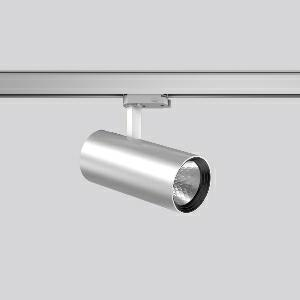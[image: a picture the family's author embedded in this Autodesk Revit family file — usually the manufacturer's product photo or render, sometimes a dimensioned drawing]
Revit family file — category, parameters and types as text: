
# Revit family: deecos_s_mini_742205_004_1_470e
name_source: partatom
category: Lighting Fixtures
units: mm (PartAtom-declared; Revit-internal decimal feet)

## family parameters
Cut with Voids When Loaded = No
Host = Face
Light Source = No
Part Type = Normal
Room Calculation Point = No
Round Connector Dimension = Use Diameter
Shared = No

## types (1)
- DEECOS S mini (1 x LED Modul 940, 3900 lm, 4000)
    Apparent Load = 29 VA
    Approval mark = CE
    CIE Flux Codes = 95 99 100 100 100
    Color Rendering = 92
    Color Temperature = 4000
    Default Elevation = 1800 mm
    Description = Series: DEECOS S mini
LED surface-mounted projector in modern design with no visible cooling ribs. Housing: die-cast aluminium, powder-coated. Rotation range: 356°. Swivel range: 90°. Black plastic ring and recessed LED to prevent glare from the side. Optical assembly with reflector made of MIRO-Silver with 98% total light reflection for outstanding efficiency - can be changed without tools. Best colour rendering index Ra>90. With multi adaptor for 3-circuit tracks 230 V. Suitable for Track on ceiling, Wall track. High quality converter without flickering and stroboscopic effect. The following accessories can be mounted without use of tools: interchangeable lenses, decorative glasses, honeycomb louvre, clear and frosted diffusers, white interchangeable plastic ring. 
Colour: silver
Diameter: 87 mm
Height: 214 mm
Lamp: LED
Socket: without socket
Colour temperature: 4000K
Colour rendering index (CRI): 92
System power: 29 W
Rated luminous flux: 3900 lm
Luminous efficiency: 134 lm/W
Control gear: Regulated power supply
Protection class: I
Type of protection: IP 20
    Height = 214 mm
    Lamp = 1 x LED Modul 940
    Lamp Light Flux = 3900 lm
    Lamp count = 1
    Length = 87 mm
    Lifetime = 50000 h
    Luminous efficacy = 134 lm/W
    Manufacturer = RZB
    ModVariant = No
    Model = 742205.004.1
    Mounting Place = Ceiling
    Mounting Type = Rail mounted
    Number of Poles = 1
    OnlyDefault = Yes
    Power Factor = 1
    Product Name = DEECOS S mini
    Product group = Track mounted projectors
    ProductGroupID = 301
    Protection Class = Protection class I
    Protection Degree = IP 20
    RLX_Detail_Level = 1
    RLX_Emergency_Light_Flux = 0 lm
    RLX_Emergency_Type = 0
    RLX_Emergency_Type_DB = No
    RlxData = <blob elided: 37689 chars, md5=e335698e>
    Socket = socket
    Standby Power = 0 W
    System Light Flux = 3900 lm
    System Power = 29 W
    Type Comments = Product without accessories
    Type Image = 741926.004.jpg
    URL = http://relux.com
    VarID = ---
    Voltage = 230 V
    Voltage Range = 220-240 V
    Weight = 0.00 kg
    Width = 0 mm  [stored 0 ft]

note: [stored X ft] marks values corroborated as IEEE doubles in the binary element streams (Revit-internal decimal feet)

## geometry (parser evidence)
native form markers: Blend x4, Sweep x12
no freeform markers — native parametric forms only
